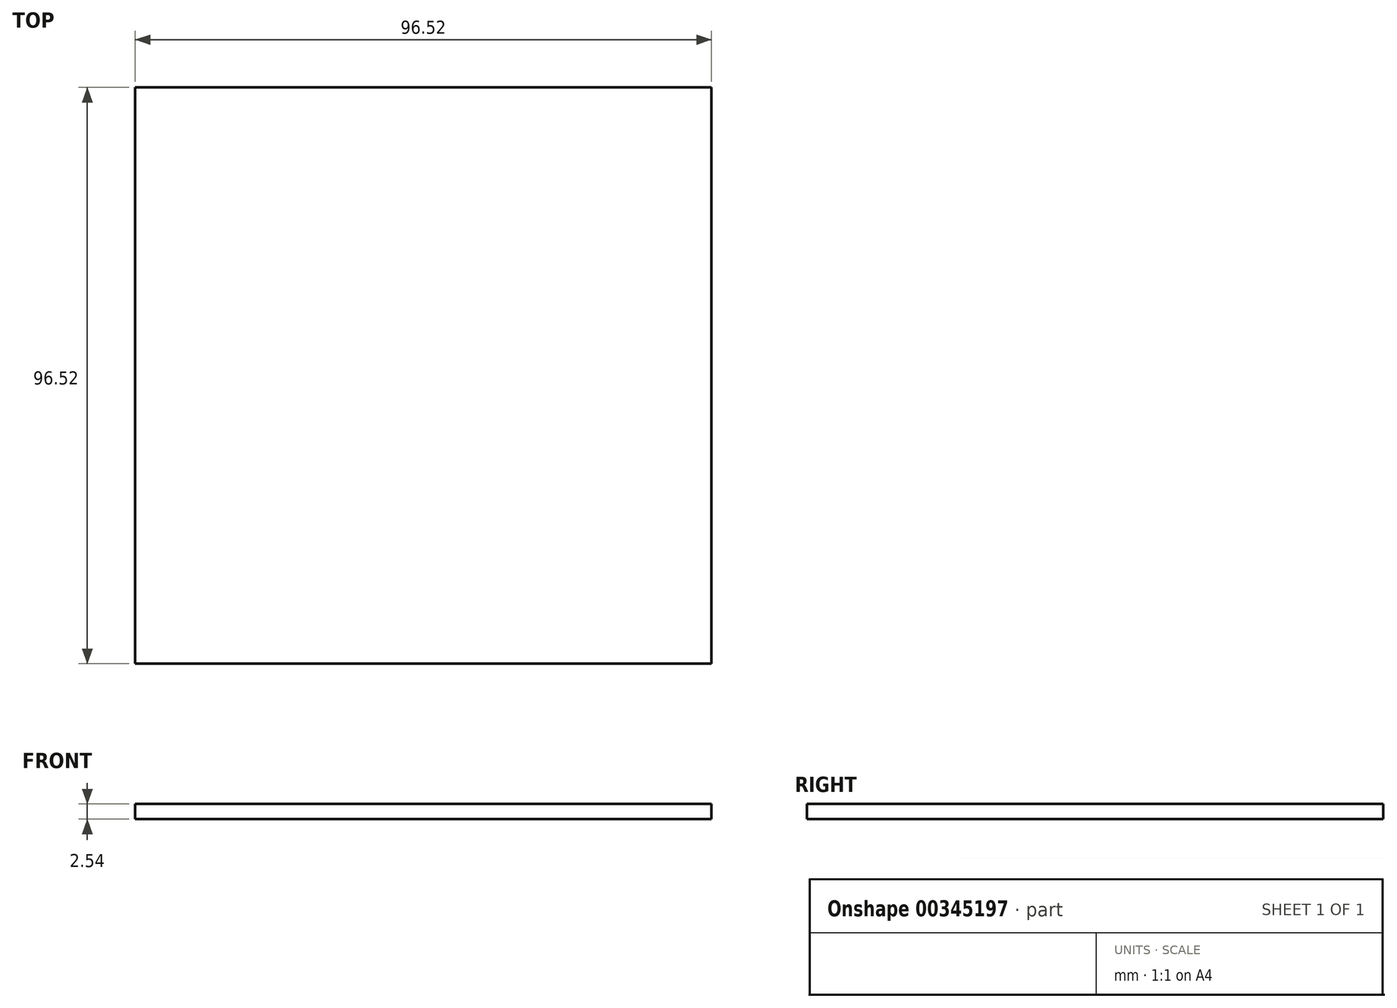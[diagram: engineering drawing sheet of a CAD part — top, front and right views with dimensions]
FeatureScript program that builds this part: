
annotation { "Feature Type Name" : "Feature", "Feature Type Description" : "" }
export const myFeature = defineFeature(function(context is Context, id is Id, definition is map)
    precondition{}
    {
        {
            var Q0;
            Q0=qCreatedBy(makeId("Top.planeOp"),FACE);
            var sketch = newSketch(context, id + "F0", { "sketchPlane" : qUnion([Q0])});
            skLineSegment(sketch, "E0.bottom", {"start": v(-48.26, -48.26) * mm, "end": v(48.26, -48.26) * mm});
            skLineSegment(sketch, "E0.top", {"start": v(-48.26, 48.26) * mm, "end": v(48.26, 48.26) * mm});
            skLineSegment(sketch, "E0.left", {"start": v(-48.26, -48.26) * mm, "end": v(-48.26, 48.26) * mm});
            skLineSegment(sketch, "E0.right", {"start": v(48.26, -48.26) * mm, "end": v(48.26, 48.26) * mm});
            skPoint(sketch, "E0.middle", {"position": v(0, 0) * mm});
            skSolve(sketch);
        }
        {
            var Q0;
            Q0=makeQuery(id+"F0.imprint","IMPRINT",FACE,{"disambiguationData":[TD([[makeQuery(id+"F0.imprint","IMPRINT",EDGE,{"derivedFrom":sQuery(id+"F0.wireOp",EDGE,"E0.bottom")}),1.0]])]});
            extrude(context, id + "F1", {"entities" : qUnion([Q0]), "endBound" : BoundingType.SYMMETRIC, "depth" : 2.54 * mm});
        }
    });
